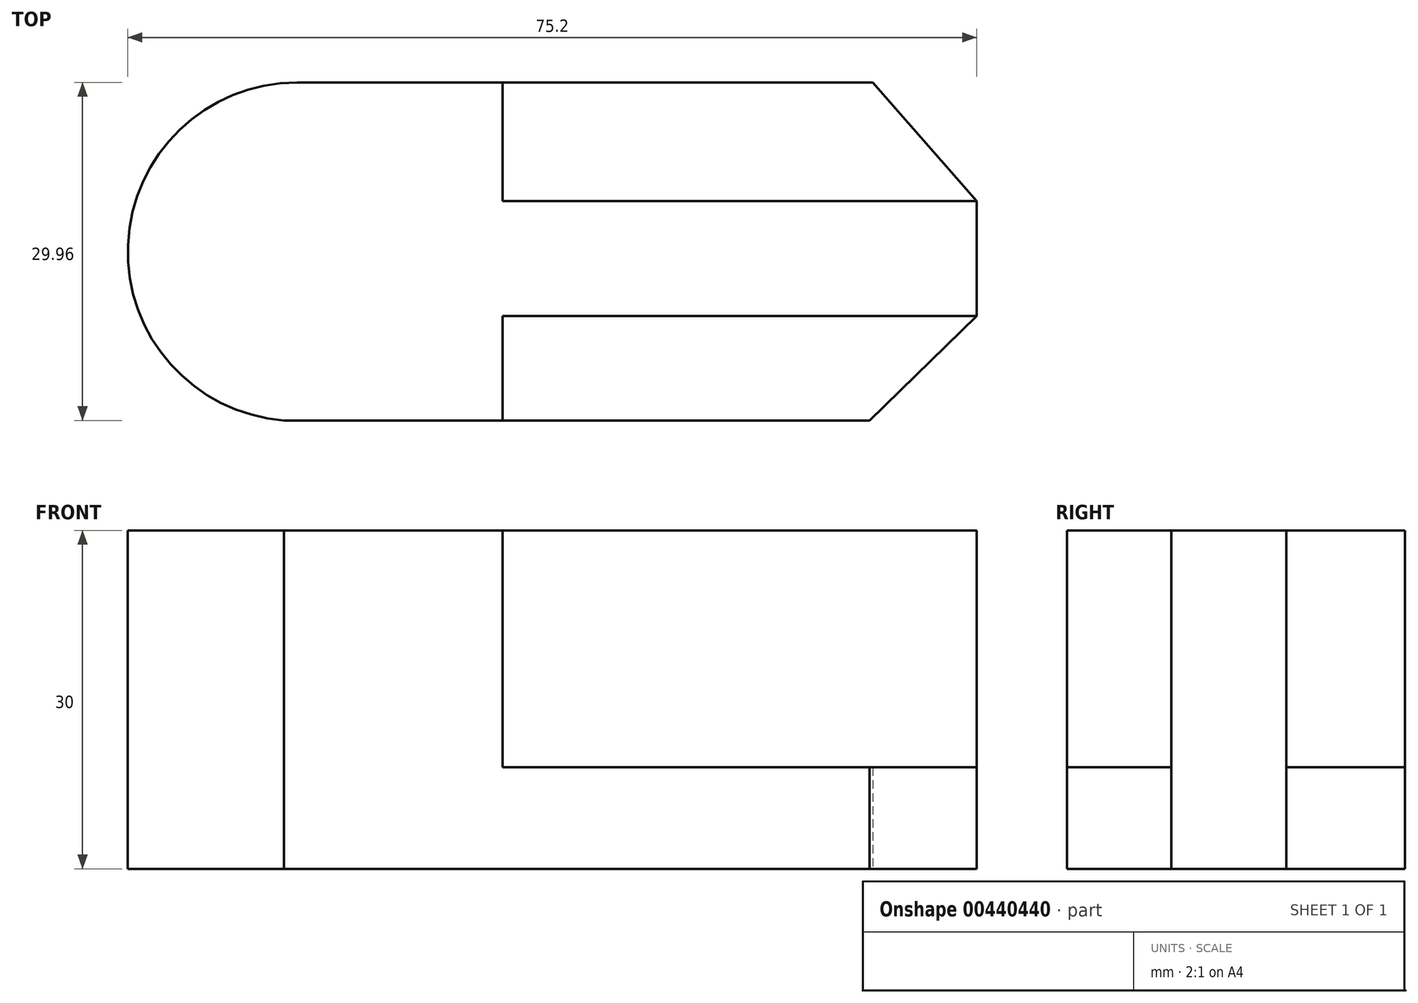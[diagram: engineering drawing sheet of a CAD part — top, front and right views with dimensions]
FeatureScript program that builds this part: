
annotation { "Feature Type Name" : "Feature", "Feature Type Description" : "" }
export const myFeature = defineFeature(function(context is Context, id is Id, definition is map)
    precondition{}
    {
        {
            var Q0;
            Q0=qCreatedBy(makeId("Top.planeOp"),FACE);
            var sketch = newSketch(context, id + "F0", { "sketchPlane" : qUnion([Q0])});
            skLineSegment(sketch, "E0", {"start": v(-3.51, 29.96) * mm, "end": v(-54.51, 29.96) * mm});
            skLineSegment(sketch, "E1", {"start": v(-3.79, 0) * mm, "end": v(-55.66, 0) * mm});
            skArc(sketch, "E2", {"start": v(-54.51, 29.96) * mm, "mid": v(-69.5, 15.53) * mm, "end": v(-55.66, 0) * mm});
            skLineSegment(sketch, "E3", {"start": v(-3.51, 29.96) * mm, "end": v(5.7, 19.45) * mm});
            skLineSegment(sketch, "E4", {"start": v(5.7, 9.25) * mm, "end": v(-3.79, 0) * mm});
            skLineSegment(sketch, "E5", {"start": v(5.7, 9.25) * mm, "end": v(5.7, 19.45) * mm});
            skSolve(sketch);
        }
        {
            var Q0;
            Q0=makeQuery(id+"F0.imprint","IMPRINT",FACE,{"disambiguationData":[TD([[makeQuery(id+"F0.imprint","IMPRINT",EDGE,{"derivedFrom":sQuery(id+"F0.wireOp",EDGE,"E0")}),1.0]])]});
            extrude(context, id + "F1", {"entities" : qUnion([Q0]), "depth" : 9 * mm});
        }
        {
            var Q0;
            Q0=makeQuery(id+"F1.opExtrude","CAP_FACE",FACE,{"disambiguationData":[OSD([sQuery(id+"F0.wireOp",EDGE,"E0"),sQuery(id+"F0.wireOp",EDGE,"E1"),sQuery(id+"F0.wireOp",EDGE,"E2"),sQuery(id+"F0.wireOp",EDGE,"E3"),sQuery(id+"F0.wireOp",EDGE,"E4"),sQuery(id+"F0.wireOp",EDGE,"E5")])],"isStart":false});
            var sketch = newSketch(context, id + "F2", { "sketchPlane" : qUnion([Q0])});
            skLineSegment(sketch, "E6", {"start": v(5.7, 19.45) * mm, "end": v(-36.3, 19.45) * mm});
            skLineSegment(sketch, "E7", {"start": v(-36.3, 19.45) * mm, "end": v(-36.3, 29.96) * mm});
            skLineSegment(sketch, "E8", {"start": v(5.7, 9.25) * mm, "end": v(-36.3, 9.25) * mm});
            skLineSegment(sketch, "E9", {"start": v(-36.3, 9.25) * mm, "end": v(-36.3, 0) * mm});
            skSolve(sketch);
        }
        {
            var Q0;
            Q0 = qSketchRegion(id + "F2", true);
            var Q1;
            Q1=makeQuery(id+"F2.imprint","IMPRINT",FACE,{"disambiguationData":[TD([[makeQuery(id+"F2.imprint","IMPRINT",EDGE,{"derivedFrom":sQuery(id+"F2.wireOp",EDGE,"E6")}),1.0]])]});
            extrude(context, id + "F3", {"entities" : qUnion([Q0, Q1]), "operationType" : NewBodyOperationType.ADD, "depth" : 21 * mm});
        }
    });
